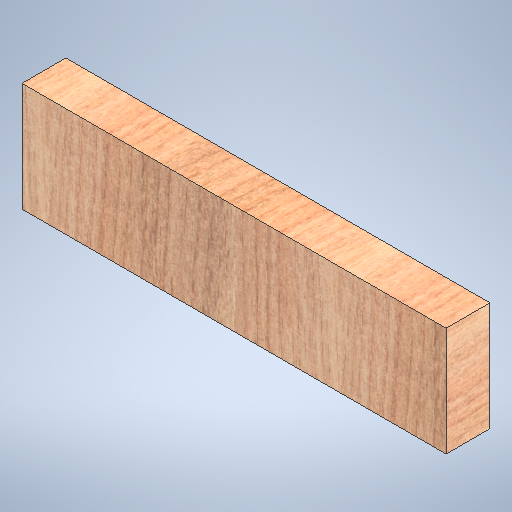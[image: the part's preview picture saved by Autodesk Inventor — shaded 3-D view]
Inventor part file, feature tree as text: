
AUTODESK INVENTOR PART (.ipt)
format: ipt  version: 2025 (Build 290162010, 162A)  size: 471,552 bytes
history: native  units: in
note: dims shown in document units (in); Inventor stores cm internally (conversion verified against a paired STEP export)
features: extrude x1, sketch x1
ambient origin geometry x8: Origin, YZ Plane, XZ Plane, XY Plane, X Axis, Y Axis, Z Axis, Center Point
bodies: Solid1 (feature_tree)
feature tree (2):
  extrude  "Extrusion1"  Depth=14.5in
  sketch  "Sketch1"  dims[d2=3.725in d3=14.5in d4=1.5in d5=0.0in]
